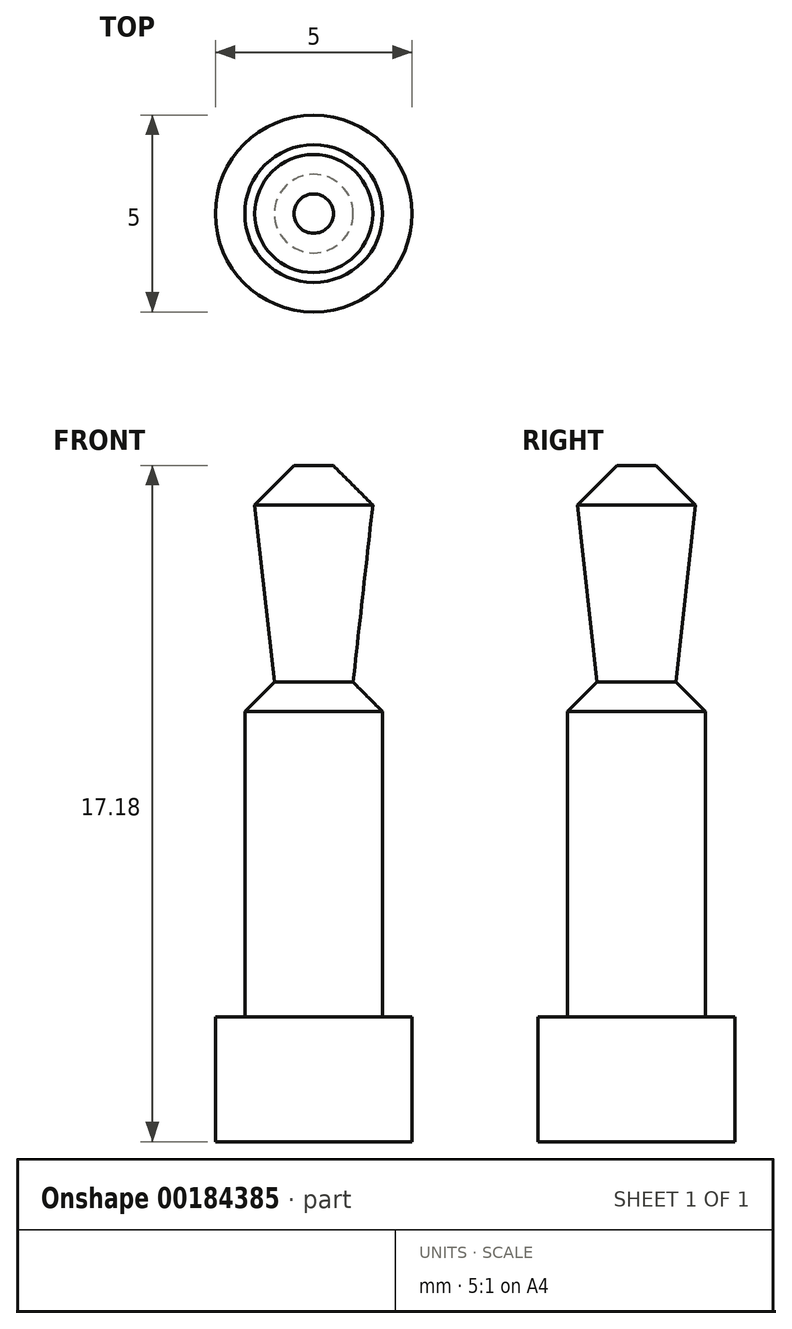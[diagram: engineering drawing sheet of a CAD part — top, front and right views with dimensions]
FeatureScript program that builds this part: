
annotation { "Feature Type Name" : "Feature", "Feature Type Description" : "" }
export const myFeature = defineFeature(function(context is Context, id is Id, definition is map)
    precondition{}
    {
        {
            var Q0;
            Q0=qCreatedBy(makeId("Top.planeOp"),FACE);
            var sketch = newSketch(context, id + "F0", { "sketchPlane" : qUnion([Q0])});
            skCircle(sketch, "E0", {"center": v(0, 0) * mm, "radius": 2.5 * mm});
            skSolve(sketch);
        }
        {
            var Q0;
            Q0 = qSketchRegion(id + "F0", true);
            extrude(context, id + "F1", {"entities" : qUnion([Q0]), "depth" : 3.17 * mm});
        }
        {
            var Q0;
            Q0=makeQuery(id+"F1.opExtrude","CAP_FACE",FACE,{"disambiguationData":[OSD([sQuery(id+"F0.wireOp",EDGE,"E0")])],"isStart":false});
            var sketch = newSketch(context, id + "F2", { "sketchPlane" : qUnion([Q0])});
            skCircle(sketch, "E1", {"center": v(0, 0) * mm, "radius": 1.75 * mm});
            skSolve(sketch);
        }
        {
            var Q0;
            Q0 = qSketchRegion(id + "F2", true);
            extrude(context, id + "F3", {"entities" : qUnion([Q0]), "operationType" : NewBodyOperationType.ADD, "depth" : 8.5 * mm});
        }
        {
            var Q0;
            Q0=makeQuery(id+"F3.opExtrude","CAP_EDGE",EDGE,{"disambiguationData":[OSD([sQuery(id+"F2.wireOp",EDGE,"E1")])],"isStart":false});
            chamfer(context, id + "F4", {"entities" : qUnion([Q0]), "width" : .75 * mm, "tangentPropagation" : true});
        }
        {
            var Q0;
            Q0=makeQuery(id+"F3.opExtrude","CAP_FACE",FACE,{"disambiguationData":[OSD([sQuery(id+"F2.wireOp",EDGE,"E1")])],"isStart":false});
            var sketch = newSketch(context, id + "F5", { "sketchPlane" : qUnion([Q0])});
            skCircle(sketch, "E2", {"center": v(0, 0) * mm, "radius": 1 * mm});
            skSolve(sketch);
        }
        {
            var Q0;
            Q0=makeQuery(id+"F5.imprint","IMPRINT",FACE,{"disambiguationData":[TD([[makeQuery(id+"F5.imprint","IMPRINT",EDGE,{"derivedFrom":sQuery(id+"F5.wireOp",EDGE,"E2")}),1.0]])]});
            cPlane(context, id + "F6", {"entities" : qUnion([Q0]), "cplaneType" : CPlaneType.OFFSET, "offset" : 4.5 * mm, "width" : 152.4 * mm, "height" : 152.4 * mm});
        }
        {
            var Q0;
            Q0=qCreatedBy(id+"F6.planeOp",FACE);
            var sketch = newSketch(context, id + "F7", { "sketchPlane" : qUnion([Q0])});
            skCircle(sketch, "E3", {"center": v(0, 0) * mm, "radius": 1.5 * mm});
            skSolve(sketch);
        }
        {
            var Q1;
            Q1=makeQuery(id+"F5.imprint","IMPRINT",FACE,{"disambiguationData":[TD([[makeQuery(id+"F5.imprint","IMPRINT",EDGE,{"derivedFrom":sQuery(id+"F5.wireOp",EDGE,"E2")}),1.0]])]});
            var Q2;
            Q2=makeQuery(id+"F7.imprint","IMPRINT",FACE,{"disambiguationData":[TD([[makeQuery(id+"F7.imprint","IMPRINT",EDGE,{"derivedFrom":sQuery(id+"F7.wireOp",EDGE,"E3")}),1.0]])]});
            loft(context, id + "F8", {"operationType" : NewBodyOperationType.ADD, "sheetProfilesArray" : [{ "sheetProfileEntities" : qUnion([Q1]) }, { "sheetProfileEntities" : qUnion([Q2]) }]});
        }
        {
            var Q0;
            Q0=makeQuery(id+"F8.opLoft","CAP_FACE",FACE,{"disambiguationData":[OSD([makeQuery(id+"F7.imprint","IMPRINT",FACE,{"disambiguationData":[TD([[makeQuery(id+"F7.imprint","IMPRINT",EDGE,{"derivedFrom":sQuery(id+"F7.wireOp",EDGE,"E3")}),1.0]])]})])],"isStart":true});
            var sketch = newSketch(context, id + "F9", { "sketchPlane" : qUnion([Q0])});
            skCircle(sketch, "E4", {"center": v(0, 0) * mm, "radius": 1.5 * mm});
            skSolve(sketch);
        }
        {
            var Q0;
            Q0 = qSketchRegion(id + "F9", true);
            extrude(context, id + "F10", {"entities" : qUnion([Q0]), "operationType" : NewBodyOperationType.ADD, "depth" : 1 * mm});
        }
        {
            var Q0;
            Q0=makeQuery(id+"F10.opExtrude","CAP_EDGE",EDGE,{"disambiguationData":[OSD([sQuery(id+"F9.wireOp",EDGE,"E4")])],"isStart":false});
            chamfer(context, id + "F11", {"entities" : qUnion([Q0]), "width" : 1 * mm, "tangentPropagation" : true});
        }
    });
